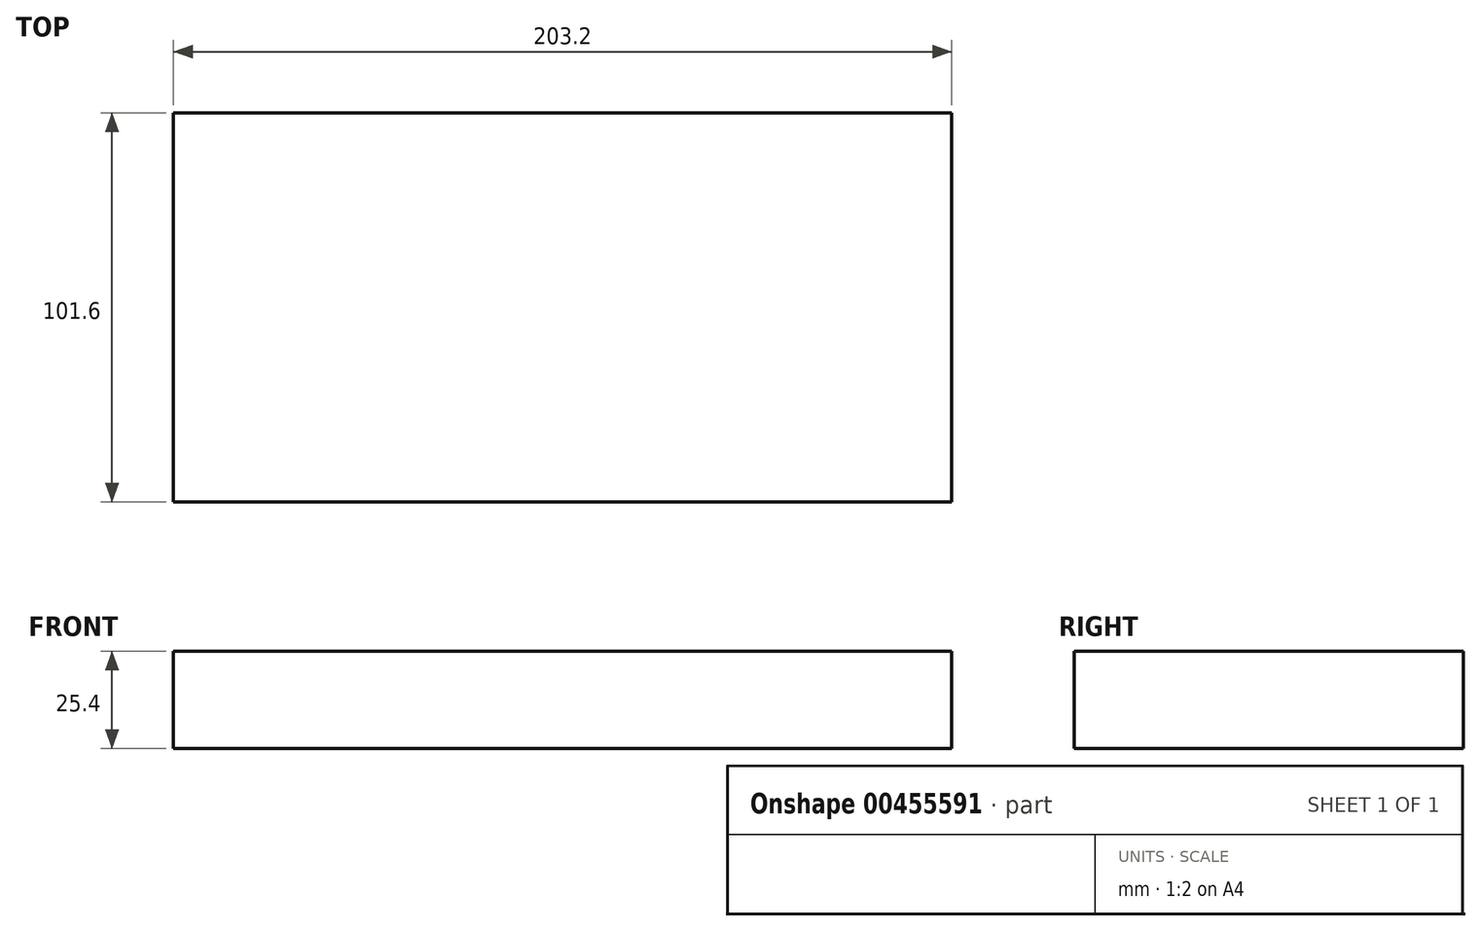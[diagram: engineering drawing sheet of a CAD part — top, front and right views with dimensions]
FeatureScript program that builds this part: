
annotation { "Feature Type Name" : "Feature", "Feature Type Description" : "" }
export const myFeature = defineFeature(function(context is Context, id is Id, definition is map)
    precondition{}
    {
        {
            var Q0;
            Q0=qCreatedBy(makeId("Top.planeOp"),FACE);
            var sketch = newSketch(context, id + "F0", { "sketchPlane" : qUnion([Q0])});
            skLineSegment(sketch, "E0.bottom", {"start": v(101.6, 50.8) * mm, "end": v(-101.6, 50.8) * mm});
            skLineSegment(sketch, "E0.top", {"start": v(101.6, -50.8) * mm, "end": v(-101.6, -50.8) * mm});
            skLineSegment(sketch, "E0.left", {"start": v(101.6, 50.8) * mm, "end": v(101.6, -50.8) * mm});
            skLineSegment(sketch, "E0.right", {"start": v(-101.6, 50.8) * mm, "end": v(-101.6, -50.8) * mm});
            skPoint(sketch, "E0.middle", {"position": v(0, 0) * mm});
            skSolve(sketch);
        }
        {
            var Q0;
            Q0 = qSketchRegion(id + "F0", true);
            extrude(context, id + "F1", {"entities" : qUnion([Q0]), "depth" : 25.4 * mm});
        }
    });
